# Revit family: ALBA_R100ExHGxxSF
name_source: partatom
category: Leuchten
units: mm (PartAtom-declared; Revit-internal decimal feet)

## family parameters
Basisbauteil = Fläche
Beim Laden mit Abzugskörper schneiden = Nein
Bemaßung runder Anschluss = Durchmesser verwenden
Gemeinsam genutzt = Nein
Lichtquelle = Ja
OmniClass-Nummer = 23.80.70.11
OmniClass-Titel = Luminaries for Internal Lighting
Raumberechnungspunkt = Nein
Teiletyp = Normal

## types (8) — shared parameters
Baugruppenkennzeichen = D5020200
Datei für fotometrisches Netz = Master_ALBA_R100E_HG_Diffusor.IES
Emissionsform beim Rendern sichtbar = Nein
Farbfilter = 16777215
Farbtemperaturverschiebung bei Dämpfen der Lampe = <Keine Auswahl>
Hersteller = RIDI Leuchten GmbH
Lampe = LED
Neigungswinkel = 90.00°
Scheinlast = 15 VA
URL = www.ridi.de
Von Kreisdurchmesser aussenden = 86 mm  [stored 0.282152 ft]
brand = RIDI
conformity mark = CE
electrical safety class = 2
height = 84 mm  [stored 0.275591 ft]
ingress protection (IP) code = IP20
length = 112 mm  [stored 0.367454 ft]
nominal frequency = 50-60Hz
nominal voltage = 230
rated input power = 15
voltage type (AC, DC, UC) = AC
weight = 0.43 kg
width = 112 mm  [stored 0.367454 ft]
zero-valued in all types: Vorgabe-Ansicht

## per-type parameters (varying)
| type | Modell |
| ALBA R100E NDHG930SF0150OS | 0322117 |
| ALBA R100E NDHG940SF0150OS | 0322118 |
| ALBA R100E DAHG930SF0150OS | 0332117 |
| ALBA R100E DAHG940SF0150OS | 0332118 |
| ALBA R100E NDHG830SF0175OS | 0322294 |
| ALBA R100E NDHG840SF0175OS | 0322295 |
| ALBA R100E DAHG830SF0175OS | 0332294 |
| ALBA R100E DAHG840SF0175OS | 0332295 |

note: column(s) folded — value = type name in every type: product name

note: [stored X ft] marks values corroborated as IEEE doubles in the binary element streams (Revit-internal decimal feet)
